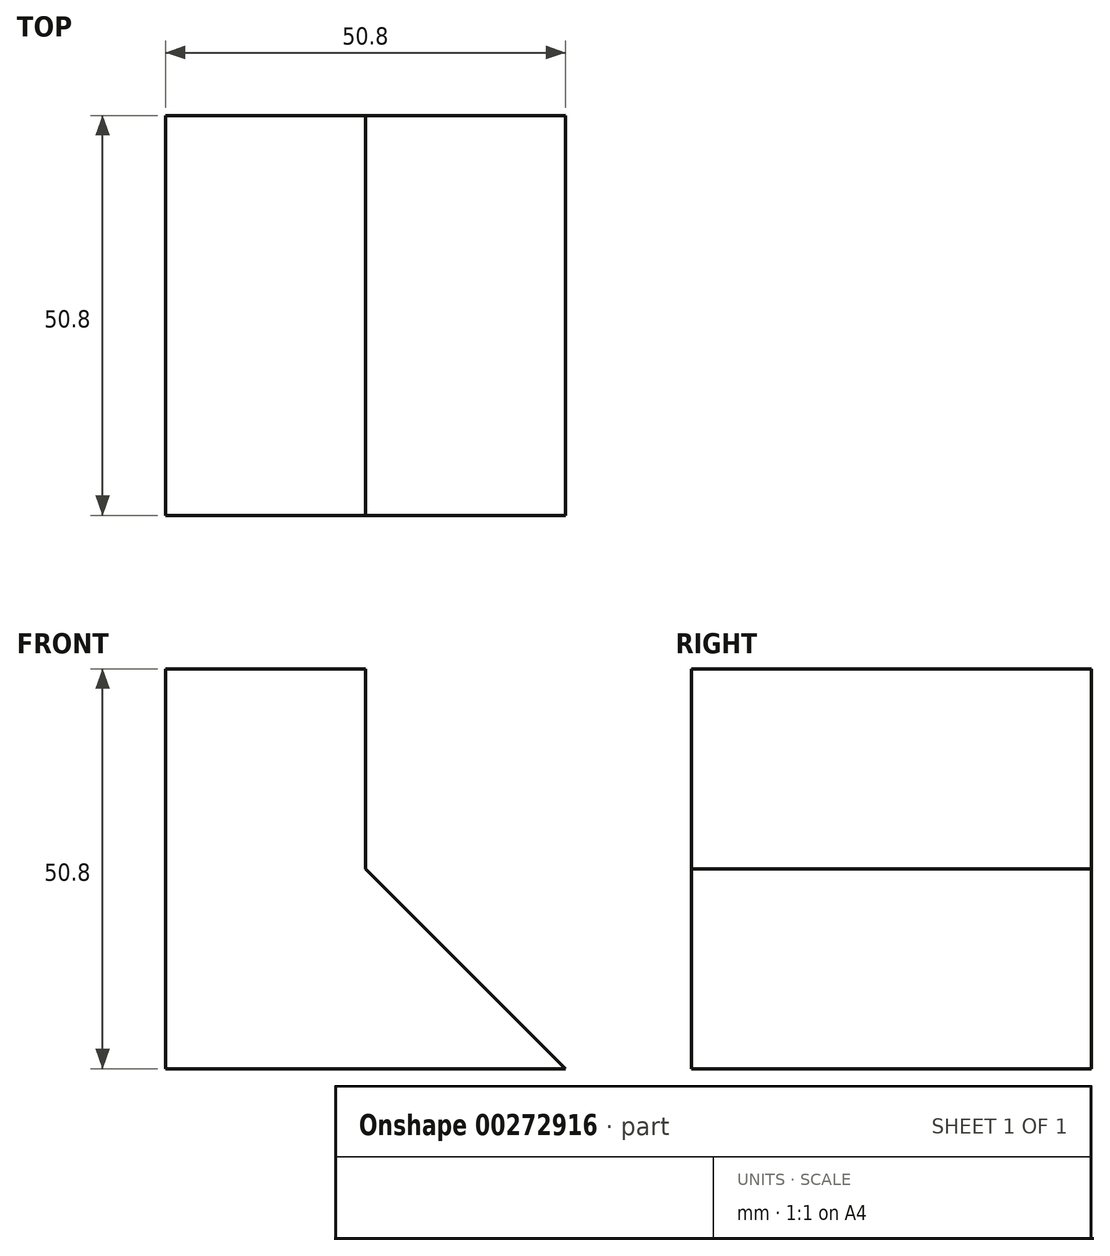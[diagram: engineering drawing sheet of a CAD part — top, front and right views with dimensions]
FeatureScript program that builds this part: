
annotation { "Feature Type Name" : "Feature", "Feature Type Description" : "" }
export const myFeature = defineFeature(function(context is Context, id is Id, definition is map)
    precondition{}
    {
        {
            var Q0;
            Q0=qCreatedBy(makeId("Front.planeOp"),FACE);
            var sketch = newSketch(context, id + "F0", { "sketchPlane" : qUnion([Q0])});
            skLineSegment(sketch, "E0", {"start": v(-57.29, 35.71) * mm, "end": v(-57.29, -15.09) * mm});
            skLineSegment(sketch, "E1", {"start": v(-57.29, -15.09) * mm, "end": v(-6.49, -15.09) * mm});
            skLineSegment(sketch, "E2", {"start": v(-57.29, 35.71) * mm, "end": v(-31.89, 35.71) * mm});
            skLineSegment(sketch, "E3", {"start": v(-31.89, 35.71) * mm, "end": v(-31.89, 10.31) * mm});
            skLineSegment(sketch, "E4", {"start": v(-31.89, 10.31) * mm, "end": v(-6.49, -15.09) * mm});
            skSolve(sketch);
        }
        {
            var Q0;
            Q0=makeQuery(id+"F0.imprint","IMPRINT",FACE,{"disambiguationData":[TD([[makeQuery(id+"F0.imprint","IMPRINT",EDGE,{"derivedFrom":sQuery(id+"F0.wireOp",EDGE,"E0")}),1.0]])]});
            extrude(context, id + "F1", {"entities" : qUnion([Q0]), "depth" : 50.8 * mm});
        }
    });
